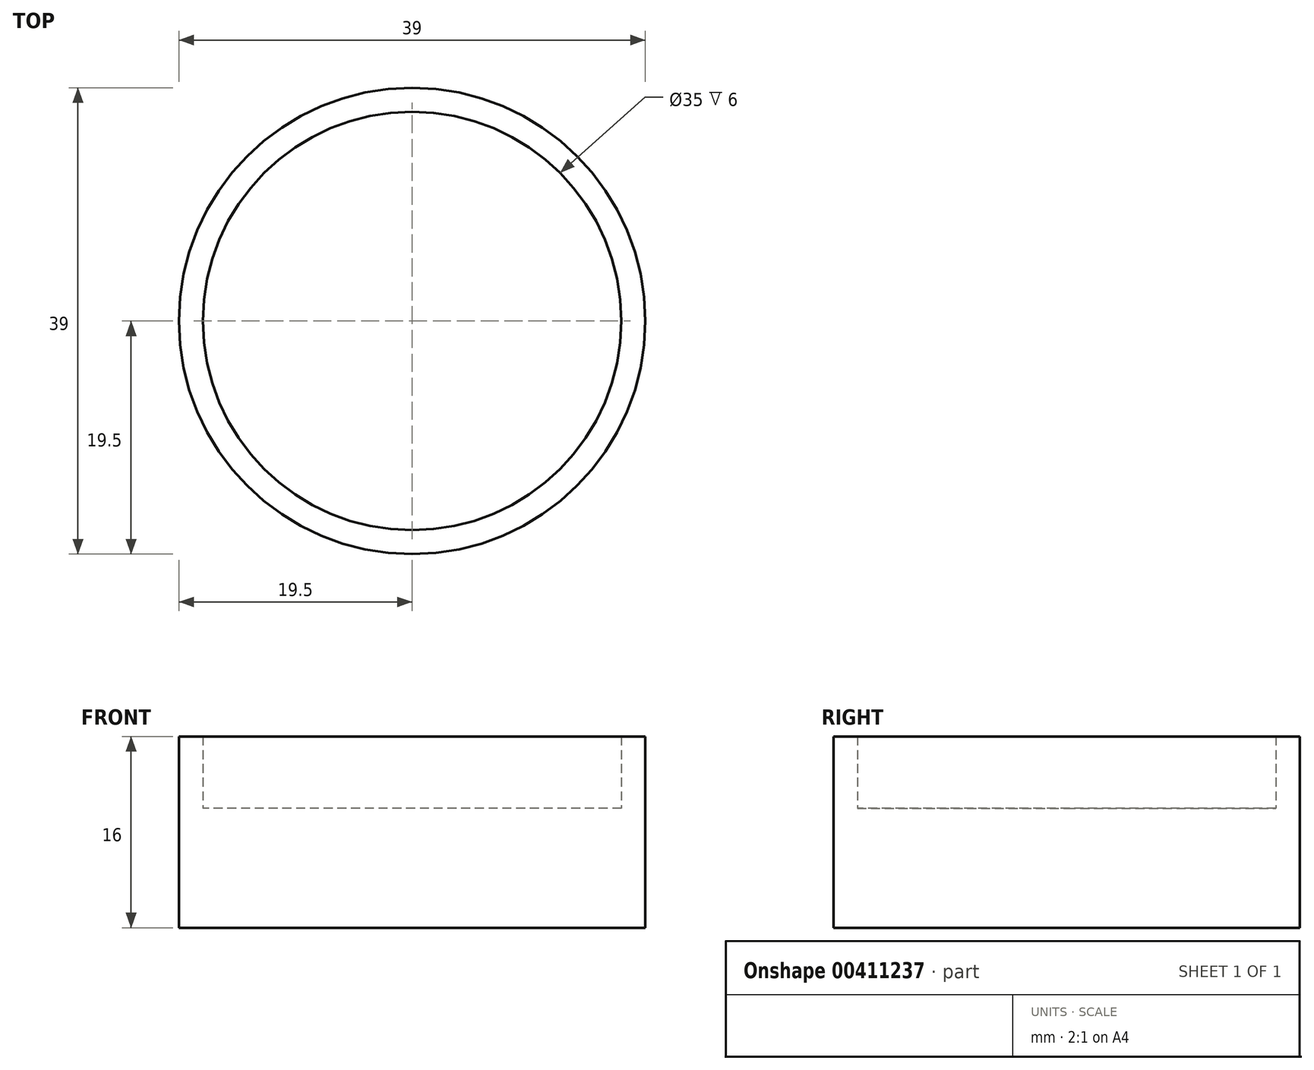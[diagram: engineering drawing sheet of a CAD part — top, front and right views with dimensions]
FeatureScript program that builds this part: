
annotation { "Feature Type Name" : "Feature", "Feature Type Description" : "" }
export const myFeature = defineFeature(function(context is Context, id is Id, definition is map)
    precondition{}
    {
        {
            var Q0;
            Q0=qCreatedBy(makeId("Top.planeOp"),FACE);
            var sketch = newSketch(context, id + "F0", { "sketchPlane" : qUnion([Q0])});
            skCircle(sketch, "E0", {"center": v(0, 0) * mm, "radius": 17.5 * mm});
            skCircle(sketch, "E1", {"center": v(0, 0) * mm, "radius": 19.5 * mm});
            skSolve(sketch);
        }
        {
            var Q0;
            Q0=makeQuery(id+"F0.imprint","IMPRINT",FACE,{"disambiguationData":[TD([[makeQuery(id+"F0.imprint","IMPRINT",EDGE,{"derivedFrom":sQuery(id+"F0.wireOp",EDGE,"E0")}),-1.0]])]});
            extrude(context, id + "F1", {"entities" : qUnion([Q0]), "depth" : (10 + 6) * mm});
        }
        {
            var Q0;
            Q0=makeQuery(id+"F0.imprint","IMPRINT",FACE,{"disambiguationData":[TD([[makeQuery(id+"F0.imprint","IMPRINT",EDGE,{"derivedFrom":sQuery(id+"F0.wireOp",EDGE,"E0")}),1.0]])]});
            extrude(context, id + "F2", {"entities" : qUnion([Q0]), "operationType" : NewBodyOperationType.ADD, "depth" : 10 * mm});
        }
    });
